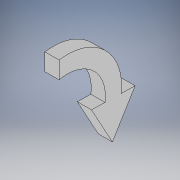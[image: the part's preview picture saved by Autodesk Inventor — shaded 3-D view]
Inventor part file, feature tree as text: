
AUTODESK INVENTOR PART (.ipt)
format: ipt  version: 2018 (Build 220112000, 112)  size: 98,816 bytes
history: native  units: in
note: dims shown in document units (in); Inventor stores cm internally (conversion verified against a paired STEP export)
features: extrude x1, sketch x1
ambient origin geometry x8: Origin, YZ Plane, XZ Plane, XY Plane, X Axis, Y Axis, Z Axis, Center Point
bodies: Solid1 (feature_tree)
feature tree (2):
  extrude  "Extrusion1"  [1 undecoded]
  sketch  "Sketch1"  dims[d0=1.0in d1=0.0in]
note: 1 required parameter value undecoded (feature->parameter linkage not recoverable at this tier; creation-order binding heuristic only, values carry confidence <= 0.55)
